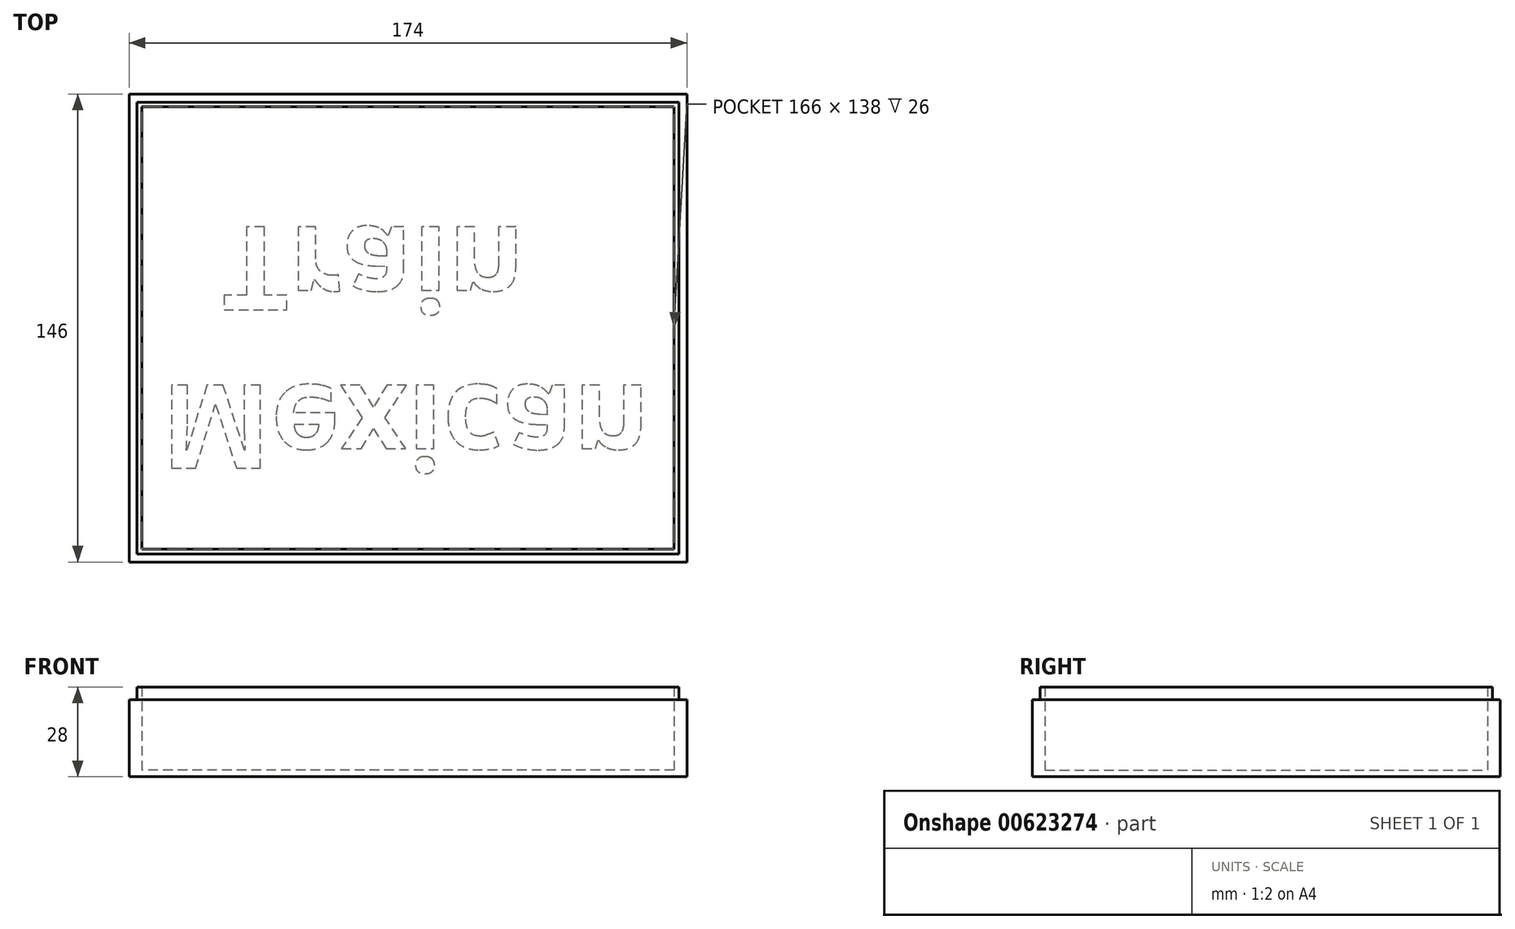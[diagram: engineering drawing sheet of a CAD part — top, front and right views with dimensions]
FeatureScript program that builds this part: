
annotation { "Feature Type Name" : "Feature", "Feature Type Description" : "" }
export const myFeature = defineFeature(function(context is Context, id is Id, definition is map)
    precondition{}
    {
        {
            var Q0;
            Q0=qCreatedBy(makeId("Top.planeOp"),FACE);
            var sketch = newSketch(context, id + "F0", { "sketchPlane" : qUnion([Q0])});
            skLineSegment(sketch, "E0.bottom", {"start": v(85, -71) * mm, "end": v(-85, -71) * mm});
            skLineSegment(sketch, "E0.top", {"start": v(85, 71) * mm, "end": v(-85, 71) * mm});
            skLineSegment(sketch, "E0.left", {"start": v(85, -71) * mm, "end": v(85, 71) * mm});
            skLineSegment(sketch, "E0.right", {"start": v(-85, -71) * mm, "end": v(-85, 71) * mm});
            skPoint(sketch, "E0.middle", {"position": v(0, 0) * mm});
            skLineSegment(sketch, "E1.bottom", {"start": v(87, -73) * mm, "end": v(-87, -73) * mm});
            skLineSegment(sketch, "E1.top", {"start": v(87, 73) * mm, "end": v(-87, 73) * mm});
            skLineSegment(sketch, "E1.left", {"start": v(87, -73) * mm, "end": v(87, 73) * mm});
            skLineSegment(sketch, "E1.right", {"start": v(-87, -73) * mm, "end": v(-87, 73) * mm});
            skSolve(sketch);
        }
        {
            var Q0;
            Q0=makeQuery(id+"F0.imprint","IMPRINT",FACE,{"disambiguationData":[TD([[makeQuery(id+"F0.imprint","IMPRINT",EDGE,{"derivedFrom":sQuery(id+"F0.wireOp",EDGE,"E0.bottom")}),-1.0]])]});
            extrude(context, id + "F1", {"entities" : qUnion([Q0]), "depth" : 2 * mm, "offsetDistance" : 25 * mm});
        }
        {
            var Q0;
            Q0=makeQuery(id+"F0.imprint","IMPRINT",FACE,{"disambiguationData":[TD([[makeQuery(id+"F0.imprint","IMPRINT",EDGE,{"derivedFrom":sQuery(id+"F0.wireOp",EDGE,"E0.bottom")}),1.0]])]});
            extrude(context, id + "F2", {"entities" : qUnion([Q0]), "operationType" : NewBodyOperationType.ADD, "depth" : 2 * mm, "offsetDistance" : 25 * mm});
        }
        {
            var Q0;
            {var subQ0=sQuery(id+"F0.wireOp",EDGE,"E0.right");var subQ1=sQuery(id+"F0.wireOp",EDGE,"E0.left");var subQ2=sQuery(id+"F0.wireOp",EDGE,"E0.top");var subQ3=sQuery(id+"F0.wireOp",EDGE,"E0.bottom");Q0=makeQuery(id+"F2.boolean.opBoolean","MERGE",FACE,{"derivedFrom":[makeQuery(id+"F1.opExtrude","CAP_FACE",FACE,{"disambiguationData":[OSD([subQ3,subQ2,subQ1,subQ0])],"isStart":false}),makeQuery(id+"F2.opExtrude","CAP_FACE",FACE,{"disambiguationData":[OSD([subQ3,subQ2,subQ1,subQ0,sQuery(id+"F0.wireOp",EDGE,"E1.bottom"),sQuery(id+"F0.wireOp",EDGE,"E1.top"),sQuery(id+"F0.wireOp",EDGE,"E1.left"),sQuery(id+"F0.wireOp",EDGE,"E1.right")])],"isStart":false})]});}
            var sketch = newSketch(context, id + "F3", { "sketchPlane" : qUnion([Q0])});
            skLineSegment(sketch, "E2.bottom", {"start": v(84.5, -70.5) * mm, "end": v(-84.5, -70.5) * mm});
            skLineSegment(sketch, "E2.top", {"start": v(84.5, 70.5) * mm, "end": v(-84.5, 70.5) * mm});
            skLineSegment(sketch, "E2.left", {"start": v(84.5, -70.5) * mm, "end": v(84.5, 70.5) * mm});
            skLineSegment(sketch, "E2.right", {"start": v(-84.5, -70.5) * mm, "end": v(-84.5, 70.5) * mm});
            skPoint(sketch, "E2.middle", {"position": v(0, 0) * mm});
            skLineSegment(sketch, "E3.bottom", {"start": v(83, -69) * mm, "end": v(-83, -69) * mm});
            skLineSegment(sketch, "E3.top", {"start": v(83, 69) * mm, "end": v(-83, 69) * mm});
            skLineSegment(sketch, "E3.left", {"start": v(83, -69) * mm, "end": v(83, 69) * mm});
            skLineSegment(sketch, "E3.right", {"start": v(-83, -69) * mm, "end": v(-83, 69) * mm});
            skSolve(sketch);
        }
        {
            var Q0;
            Q0=makeQuery(id+"F3.imprint","IMPRINT",FACE,{"disambiguationData":[TD([[makeQuery(id+"F3.imprint","IMPRINT",EDGE,{"derivedFrom":sQuery(id+"F3.wireOp",EDGE,"E2.bottom")}),-1.0]])]});
            extrude(context, id + "F4", {"entities" : qUnion([Q0]), "operationType" : NewBodyOperationType.ADD, "depth" : 26 * mm, "offsetDistance" : 25 * mm});
        }
        {
            var Q0;
            {var subQ0=sQuery(id+"F0.wireOp",EDGE,"E0.right");var subQ1=sQuery(id+"F0.wireOp",EDGE,"E0.left");var subQ2=sQuery(id+"F0.wireOp",EDGE,"E0.top");var subQ3=sQuery(id+"F0.wireOp",EDGE,"E0.bottom");Q0=makeQuery(id+"F2.boolean.opBoolean","MERGE",FACE,{"derivedFrom":[makeQuery(id+"F1.opExtrude","CAP_FACE",FACE,{"disambiguationData":[OSD([subQ3,subQ2,subQ1,subQ0])],"isStart":true}),makeQuery(id+"F2.opExtrude","CAP_FACE",FACE,{"disambiguationData":[OSD([subQ3,subQ2,subQ1,subQ0,sQuery(id+"F0.wireOp",EDGE,"E1.bottom"),sQuery(id+"F0.wireOp",EDGE,"E1.top"),sQuery(id+"F0.wireOp",EDGE,"E1.left"),sQuery(id+"F0.wireOp",EDGE,"E1.right")])],"isStart":true})]});}
            var sketch = newSketch(context, id + "F5", { "sketchPlane" : qUnion([Q0])});
            skLineSegment(sketch, "E4", {"start": v(-77, 73) * mm, "end": v(-77, -73) * mm, "construction": true});
            skLineSegment(sketch, "E5", {"start": v(-87, 48) * mm, "end": v(87, 48) * mm, "construction": true});
            skText(sketch, "E6", { "text": "Mexican\n  Train", "fontName": "OpenSans-Bold.ttf"});
            skLineSegment(sketch, "E7", {"start": v(-87, 56.62) * mm, "end": v(-77, 56.62) * mm, "construction": true});
            skLineSegment(sketch, "E8", {"start": v(-68.03, 73) * mm, "end": v(-68.03, 48) * mm, "construction": true});
            const initialGuessF5  = {"E6": [-0.077, 0.01783, 1, 0, 0.02617]};
            skSetInitialGuess(sketch, initialGuessF5);
            skSolve(sketch);
        }
        {
            var Q0;
            Q0=makeQuery(id+"F5.imprint","IMPRINT",FACE,{"disambiguationData":[TD([[makeQuery(id+"F5.imprint","IMPRINT",EDGE,{"derivedFrom":sQuery(id+"F5.wireOp",EDGE,"E6.sketch_text.stroke-0")}),-1.0]])]});
            var Q1;
            Q1=makeQuery(id+"F5.imprint","IMPRINT",FACE,{"disambiguationData":[TD([[makeQuery(id+"F5.imprint","IMPRINT",EDGE,{"derivedFrom":sQuery(id+"F5.wireOp",EDGE,"E6.sketch_text.stroke-19")}),-1.0]])]});
            var Q2;
            Q2=makeQuery(id+"F5.imprint","IMPRINT",FACE,{"disambiguationData":[TD([[makeQuery(id+"F5.imprint","IMPRINT",EDGE,{"derivedFrom":sQuery(id+"F5.wireOp",EDGE,"E6.sketch_text.stroke-39")}),-1.0]])]});
            var Q3;
            Q3=makeQuery(id+"F5.imprint","IMPRINT",FACE,{"disambiguationData":[TD([[makeQuery(id+"F5.imprint","IMPRINT",EDGE,{"derivedFrom":sQuery(id+"F5.wireOp",EDGE,"E6.sketch_text.stroke-56")}),-1.0]])]});
            var Q4;
            Q4=makeQuery(id+"F5.imprint","IMPRINT",FACE,{"disambiguationData":[TD([[makeQuery(id+"F5.imprint","IMPRINT",EDGE,{"derivedFrom":sQuery(id+"F5.wireOp",EDGE,"E6.sketch_text.stroke-51")}),-1.0]])]});
            var Q5;
            Q5=makeQuery(id+"F5.imprint","IMPRINT",FACE,{"disambiguationData":[TD([[makeQuery(id+"F5.imprint","IMPRINT",EDGE,{"derivedFrom":sQuery(id+"F5.wireOp",EDGE,"E6.sketch_text.stroke-60")}),-1.0]])]});
            var Q6;
            Q6=makeQuery(id+"F5.imprint","IMPRINT",FACE,{"disambiguationData":[TD([[makeQuery(id+"F5.imprint","IMPRINT",EDGE,{"derivedFrom":sQuery(id+"F5.wireOp",EDGE,"E6.sketch_text.stroke-74")}),-1.0]])]});
            var Q7;
            Q7=makeQuery(id+"F5.imprint","IMPRINT",FACE,{"disambiguationData":[TD([[makeQuery(id+"F5.imprint","IMPRINT",EDGE,{"derivedFrom":sQuery(id+"F5.wireOp",EDGE,"E6.sketch_text.stroke-99")}),-1.0]])]});
            var Q8;
            Q8=makeQuery(id+"F5.imprint","IMPRINT",FACE,{"disambiguationData":[TD([[makeQuery(id+"F5.imprint","IMPRINT",EDGE,{"derivedFrom":sQuery(id+"F5.wireOp",EDGE,"E6.sketch_text.stroke-116")}),-1.0]])]});
            var Q9;
            Q9=makeQuery(id+"F5.imprint","IMPRINT",FACE,{"disambiguationData":[TD([[makeQuery(id+"F5.imprint","IMPRINT",EDGE,{"derivedFrom":sQuery(id+"F5.wireOp",EDGE,"E6.sketch_text.stroke-124")}),-1.0]])]});
            var Q10;
            Q10=makeQuery(id+"F5.imprint","IMPRINT",FACE,{"disambiguationData":[TD([[makeQuery(id+"F5.imprint","IMPRINT",EDGE,{"derivedFrom":sQuery(id+"F5.wireOp",EDGE,"E6.sketch_text.stroke-137")}),-1.0]])]});
            var Q11;
            Q11=makeQuery(id+"F5.imprint","IMPRINT",FACE,{"disambiguationData":[TD([[makeQuery(id+"F5.imprint","IMPRINT",EDGE,{"derivedFrom":sQuery(id+"F5.wireOp",EDGE,"E6.sketch_text.stroke-167")}),-1.0]])]});
            var Q12;
            Q12=makeQuery(id+"F5.imprint","IMPRINT",FACE,{"disambiguationData":[TD([[makeQuery(id+"F5.imprint","IMPRINT",EDGE,{"derivedFrom":sQuery(id+"F5.wireOp",EDGE,"E6.sketch_text.stroke-162")}),-1.0]])]});
            var Q13;
            Q13=makeQuery(id+"F5.imprint","IMPRINT",FACE,{"disambiguationData":[TD([[makeQuery(id+"F5.imprint","IMPRINT",EDGE,{"derivedFrom":sQuery(id+"F5.wireOp",EDGE,"E6.sketch_text.stroke-171")}),-1.0]])]});
            extrude(context, id + "F6", {"entities" : qUnion([Q0, Q1, Q2, Q3, Q4, Q5, Q6, Q7, Q8, Q9, Q10, Q11, Q12, Q13]), "operationType" : NewBodyOperationType.REMOVE, "oppositeDirection" : true, "depth" : .1 * mm, "offsetDistance" : 25 * mm});
        }
        {
            var Q0;
            {var subQ0=sQuery(id+"F0.wireOp",EDGE,"E1.right");var subQ1=sQuery(id+"F0.wireOp",EDGE,"E1.left");var subQ2=sQuery(id+"F0.wireOp",EDGE,"E1.top");var subQ3=sQuery(id+"F0.wireOp",EDGE,"E1.bottom");var subQ4=sQuery(id+"F0.wireOp",EDGE,"E0.right");var subQ5=sQuery(id+"F0.wireOp",EDGE,"E0.left");var subQ6=sQuery(id+"F0.wireOp",EDGE,"E0.top");var subQ7=sQuery(id+"F0.wireOp",EDGE,"E0.bottom");Q0=makeQuery(id+"F4.boolean.opBoolean","SPLIT",FACE,{"disambiguationData":[TD([makeQuery(id+"F2.opExtrude","SWEPT_FACE",FACE,{"disambiguationData":[OSD([subQ3])]})])],"derivedFrom":makeQuery(id+"F2.boolean.opBoolean","MERGE",FACE,{"derivedFrom":[makeQuery(id+"F1.opExtrude","CAP_FACE",FACE,{"disambiguationData":[OSD([subQ7,subQ6,subQ5,subQ4])],"isStart":false}),makeQuery(id+"F2.opExtrude","CAP_FACE",FACE,{"disambiguationData":[OSD([subQ7,subQ6,subQ5,subQ4,subQ3,subQ2,subQ1,subQ0])],"isStart":false})]})});}
            extrude(context, id + "F7", {"entities" : qUnion([Q0]), "operationType" : NewBodyOperationType.ADD, "depth" : 22 * mm, "offsetDistance" : 25 * mm});
        }
    });
